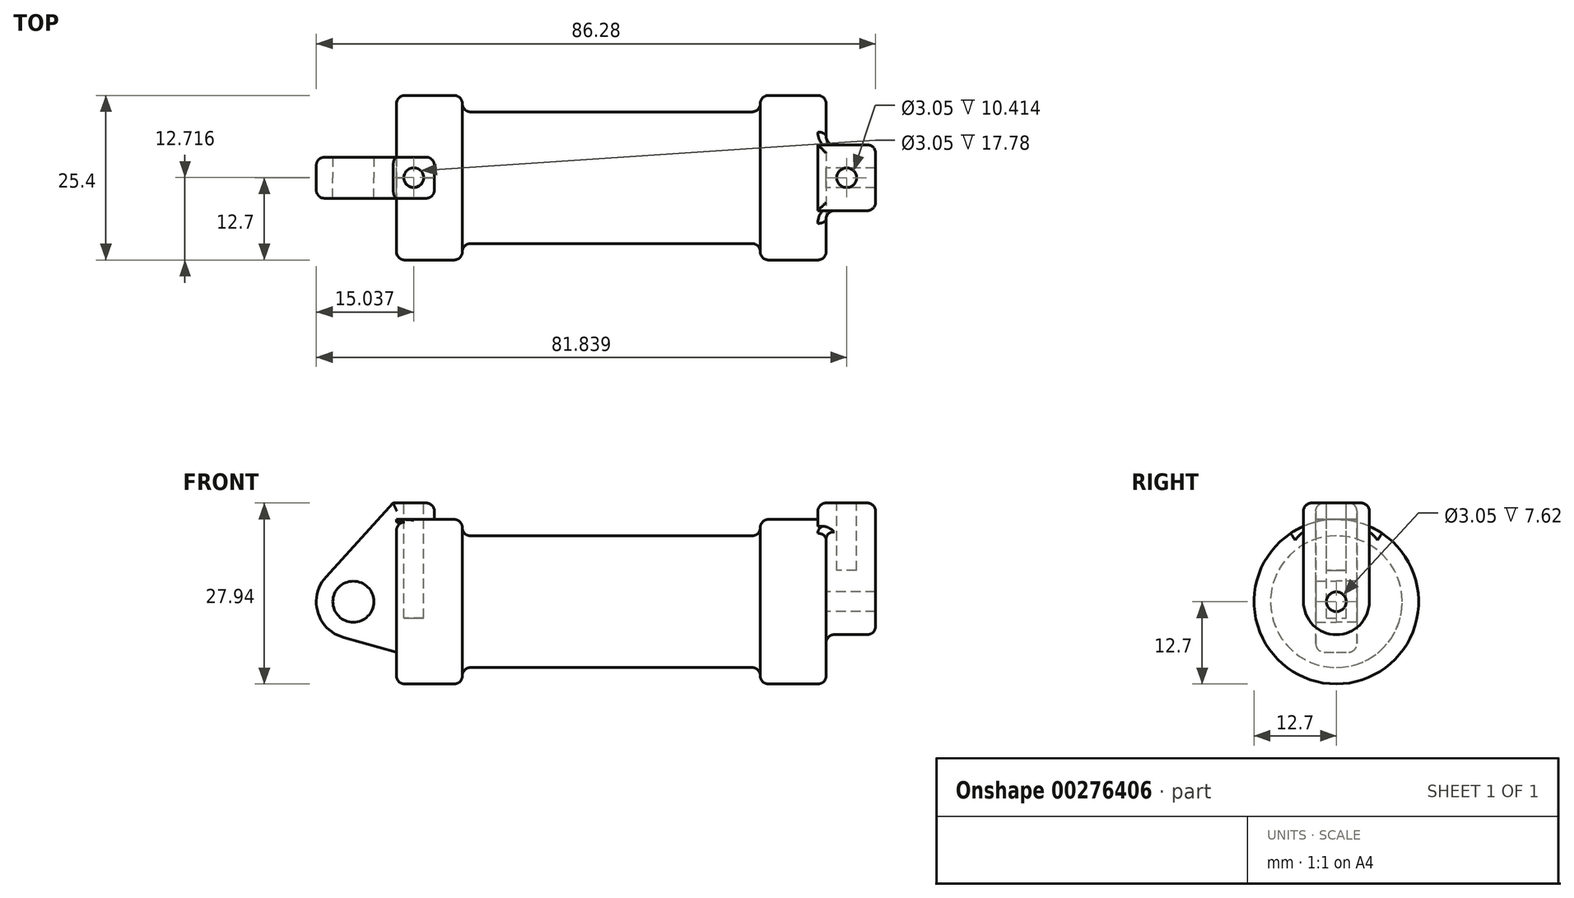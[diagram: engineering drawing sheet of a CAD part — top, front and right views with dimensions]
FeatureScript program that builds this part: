
annotation { "Feature Type Name" : "Feature", "Feature Type Description" : "" }
export const myFeature = defineFeature(function(context is Context, id is Id, definition is map)
    precondition{}
    {
        {
            var Q0;
            Q0=qCreatedBy(makeId("Front.planeOp"),FACE);
            var sketch = newSketch(context, id + "F0", { "sketchPlane" : qUnion([Q0])});
            skLineSegment(sketch, "E0", {"start": v(0, 0) * mm, "end": v(0, 12.7) * mm});
            skLineSegment(sketch, "E1", {"start": v(0, 12.7) * mm, "end": v(10.16, 12.7) * mm});
            skLineSegment(sketch, "E2", {"start": v(10.16, 12.7) * mm, "end": v(10.16, 10.16) * mm});
            skLineSegment(sketch, "E3", {"start": v(10.16, 10.16) * mm, "end": v(56.13, 10.16) * mm});
            skLineSegment(sketch, "E4", {"start": v(56.13, 10.16) * mm, "end": v(56.13, 12.7) * mm});
            skLineSegment(sketch, "E5", {"start": v(56.13, 12.7) * mm, "end": v(66.3, 12.7) * mm});
            skLineSegment(sketch, "E6", {"start": v(66.3, 12.7) * mm, "end": v(66.3, 0) * mm});
            skLineSegment(sketch, "E7", {"start": v(66.3, 0) * mm, "end": v(0, 0) * mm});
            skLineSegment(sketch, "E8", {"start": v(5.84, 15.24) * mm, "end": v(-0.5, 15.24) * mm});
            skLineSegment(sketch, "E9", {"start": v(-0.5, 15.24) * mm, "end": v(-10.88, 3.85) * mm});
            skLineSegment(sketch, "E10", {"start": v(0, 0) * mm, "end": v(-6.65, 0) * mm});
            skCircle(sketch, "E11", {"center": v(-6.65, 0) * mm, "radius": 5.72 * mm});
            skCircle(sketch, "E12", {"center": v(-6.65, 0) * mm, "radius": 3.18 * mm});
            skLineSegment(sketch, "E13", {"start": v(5.84, 15.24) * mm, "end": v(5.84, -9.4) * mm});
            skLineSegment(sketch, "E14", {"start": v(5.84, -9.4) * mm, "end": v(-8.18, -5.5) * mm});
            skSolve(sketch);
        }
        {
            var Q0;
            {var subQ0=sQuery(id+"F0.wireOp",EDGE,"E2");Q0=makeQuery(id+"F0.imprint","IMPRINT",FACE,{"disambiguationData":[TD([[makeQuery(id+"F0.imprint","IMPRINT",EDGE,{"derivedFrom":subQ0}),-1.0]])]});}
            var Q1;
            {var subQ0=sQuery(id+"F0.wireOp",EDGE,"E0");Q1=makeQuery(id+"F0.imprint","IMPRINT",FACE,{"disambiguationData":[TD([[makeQuery(id+"F0.imprint","IMPRINT",EDGE,{"derivedFrom":subQ0}),-1.0]])]});}
            var Q2;
            Q2=sQuery(id+"F0.wireOp",EDGE,"E7");
            revolve(context, id + "F1", {"entities" : qUnion([Q0, Q1]), "axis" : qUnion([Q2]), "revolveType" : RevolveType.FULL});
        }
        {
            var Q0;
            Q0=makeQuery(id+"F0.imprint","IMPRINT",FACE,{"disambiguationData":[TD([[makeQuery(id+"F0.imprint","IMPRINT",EDGE,{"derivedFrom":sQuery(id+"F0.wireOp",EDGE,"E12")}),-1.0]])]});
            var Q1;
            {var subQ0=sQuery(id+"F0.wireOp",EDGE,"E14");Q1=makeQuery(id+"F0.imprint","IMPRINT",FACE,{"disambiguationData":[TD([[makeQuery(id+"F0.imprint","IMPRINT",EDGE,{"derivedFrom":subQ0}),-1.0]])]});}
            var Q2;
            {var subQ1=sQuery(id+"F0.wireOp",EDGE,"E0");Q2=makeQuery(id+"F0.imprint","IMPRINT",FACE,{"disambiguationData":[TD([[makeQuery(id+"F0.imprint","IMPRINT",EDGE,{"derivedFrom":subQ1}),1.0]])]});}
            extrude(context, id + "F2", {"entities" : qUnion([Q0, Q1, Q2]), "operationType" : NewBodyOperationType.ADD, "endBound" : BoundingType.SYMMETRIC, "depth" : 6.35 * mm, "hasDraft" : true, "draftAngle" : 0.1 * degree, "hasSecondDirection" : true, "secondDirectionOppositeDirection" : true, "secondDirectionDepth" : 25.4 * mm});
        }
        {
            var Q0;
            Q0=makeQuery(id+"F1.opRevolve","SWEPT_FACE",FACE,{"disambiguationData":[OSD([sQuery(id+"F0.wireOp",EDGE,"E6")])]});
            var sketch = newSketch(context, id + "F3", { "sketchPlane" : qUnion([Q0])});
            skCircle(sketch, "E15", {"center": v(0, 0) * mm, "radius": 1.52 * mm});
            skCircle(sketch, "E16", {"center": v(0, 0) * mm, "radius": 5.08 * mm});
            skLineSegment(sketch, "E17", {"start": v(-5.08, 0) * mm, "end": v(-5.08, 15.24) * mm});
            skLineSegment(sketch, "E18", {"start": v(5.08, 0) * mm, "end": v(5.08, 15.24) * mm});
            skLineSegment(sketch, "E19", {"start": v(-5.08, 15.24) * mm, "end": v(5.08, 15.24) * mm});
            skSolve(sketch);
        }
        {
            var Q0;
            {var subQ0=sQuery(id+"F3.wireOp",EDGE,"E17");var subQ1=sQuery(id+"F3.wireOp",EDGE,"E16");var subQ2=makeQuery(id+"F3.imprint","INTERSECT",VERTEX,{"derivedFrom":[subQ1,subQ0]});Q0=makeQuery(id+"F3.imprint","IMPRINT",FACE,{"disambiguationData":[TD([[makeQuery(id+"F3.imprint","IMPRINT",EDGE,{"disambiguationData":[TD([[subQ2,1.0]])],"derivedFrom":subQ1}),-1.0]])]});}
            var Q1;
            {var subQ0=sQuery(id+"F3.wireOp",EDGE,"E19");Q1=makeQuery(id+"F3.imprint","IMPRINT",FACE,{"disambiguationData":[TD([[makeQuery(id+"F3.imprint","IMPRINT",EDGE,{"derivedFrom":subQ0}),-1.0]])]});}
            var Q2;
            Q2=makeQuery(id+"F3.imprint","IMPRINT",FACE,{"disambiguationData":[TD([[makeQuery(id+"F3.imprint","IMPRINT",EDGE,{"derivedFrom":sQuery(id+"F3.wireOp",EDGE,"E15")}),-1.0]])]});
            extrude(context, id + "F4", {"entities" : qUnion([Q0, Q1, Q2]), "operationType" : NewBodyOperationType.ADD, "depth" : 7.62 * mm});
        }
        {
            var Q0;
            Q0=makeQuery(id+"F4.opExtrude","CAP_FACE",FACE,{"disambiguationData":[OSD([sQuery(id+"F3.wireOp",EDGE,"E15"),sQuery(id+"F3.wireOp",EDGE,"E16"),sQuery(id+"F3.wireOp",EDGE,"E17"),sQuery(id+"F3.wireOp",EDGE,"E18"),sQuery(id+"F3.wireOp",EDGE,"E19")])],"isStart":true});
            extrude(context, id + "F5", {"entities" : qUnion([Q0]), "operationType" : NewBodyOperationType.ADD, "depth" : 1.27 * mm});
        }
        {
            var Q0;
            {var subQ0=sQuery(id+"F3.wireOp",EDGE,"E19");Q0=makeQuery(id+"F5.boolean.opBoolean","MERGE",FACE,{"derivedFrom":[makeQuery(id+"F4.opExtrude","SWEPT_FACE",FACE,{"disambiguationData":[OSD([subQ0])]}),makeQuery(id+"F5.opExtrude","SWEPT_FACE",FACE,{"disambiguationData":[OSD([subQ0])]})]});}
            var sketch = newSketch(context, id + "F6", { "sketchPlane" : qUnion([Q0])});
            skCircle(sketch, "E20", {"center": v(69.47, 0) * mm, "radius": 1.52 * mm});
            skSolve(sketch);
        }
        {
            var Q0;
            Q0=makeQuery(id+"F6.imprint","IMPRINT",FACE,{"disambiguationData":[TD([[makeQuery(id+"F6.imprint","IMPRINT",EDGE,{"derivedFrom":sQuery(id+"F6.wireOp",EDGE,"E20")}),1.0]])]});
            extrude(context, id + "F7", {"entities" : qUnion([Q0]), "operationType" : NewBodyOperationType.REMOVE, "oppositeDirection" : true, "depth" : 10.4 * mm});
        }
        {
            var Q0;
            Q0=makeQuery(id+"F1.opRevolve","SWEPT_EDGE",EDGE,{"disambiguationData":[OSD([sQuery(id+"F0.wireOp",EDGE,"E3"),sQuery(id+"F0.wireOp",EDGE,"E4")])]});
            var Q1;
            Q1=makeQuery(id+"F1.opRevolve","SWEPT_EDGE",EDGE,{"disambiguationData":[OSD([sQuery(id+"F0.wireOp",EDGE,"E4"),sQuery(id+"F0.wireOp",EDGE,"E5")])]});
            var Q2;
            Q2=makeQuery(id+"F5.opExtrude","CAP_EDGE",EDGE,{"disambiguationData":[OSD([sQuery(id+"F0.wireOp",EDGE,"E5"),sQuery(id+"F0.wireOp",EDGE,"E6")])],"isStart":false});
            var Q3;
            {var subQ0=sQuery(id+"F3.wireOp",EDGE,"E17");var subQ1=sQuery(id+"F3.wireOp",EDGE,"E19");var subQ2=sQuery(id+"F3.wireOp",EDGE,"E18");var subQ3=sQuery(id+"F3.wireOp",EDGE,"E16");var subQ4=sQuery(id+"F3.wireOp",EDGE,"E15");var subQ5=sQuery(id+"F0.wireOp",EDGE,"E6");var subQ6=sQuery(id+"F0.wireOp",EDGE,"E5");Q3=makeQuery(id+"F5.opExtrude","SWEPT_EDGE",EDGE,{"disambiguationData":[OSD([subQ6,subQ5,subQ4,subQ3,subQ0,subQ2,subQ1]),TDD([makeQuery(id+"F4.boolean.opBoolean","TWEAK_VERTEX",VERTEX,{"derivedFrom":[makeQuery(id+"F1.opRevolve","SWEPT_FACE",FACE,{"disambiguationData":[OSD([subQ6])]}),makeQuery(id+"F1.opRevolve","SWEPT_FACE",FACE,{"disambiguationData":[OSD([subQ5])]}),makeQuery(id+"F4.opExtrude","CAP_FACE",FACE,{"disambiguationData":[OSD([subQ4,subQ3,subQ0,subQ2,subQ1])],"isStart":true}),makeQuery(id+"F4.opExtrude","SWEPT_FACE",FACE,{"disambiguationData":[OSD([subQ0])]})]})])]});}
            var Q4;
            {var subQ0=sQuery(id+"F3.wireOp",EDGE,"E16");var subQ1=sQuery(id+"F3.wireOp",EDGE,"E17");Q4=makeQuery(id+"F4.boolean.opBoolean","SPLIT",EDGE,{"disambiguationData":[TD([makeQuery(id+"F4.opExtrude","SWEPT_FACE",FACE,{"disambiguationData":[OSD([subQ0])]})])],"derivedFrom":makeQuery(id+"F4.opExtrude","CAP_EDGE",EDGE,{"disambiguationData":[OSD([subQ1])],"isStart":true})});}
            var Q5;
            Q5=makeQuery(id+"F4.opExtrude","CAP_EDGE",EDGE,{"disambiguationData":[OSD([sQuery(id+"F3.wireOp",EDGE,"E16")])],"isStart":true});
            var Q6;
            {var subQ0=sQuery(id+"F3.wireOp",EDGE,"E16");var subQ1=sQuery(id+"F3.wireOp",EDGE,"E18");Q6=makeQuery(id+"F4.boolean.opBoolean","SPLIT",EDGE,{"disambiguationData":[TD([makeQuery(id+"F4.opExtrude","SWEPT_FACE",FACE,{"disambiguationData":[OSD([subQ0])]})])],"derivedFrom":makeQuery(id+"F4.opExtrude","CAP_EDGE",EDGE,{"disambiguationData":[OSD([subQ1])],"isStart":true})});}
            var Q7;
            {var subQ0=sQuery(id+"F3.wireOp",EDGE,"E18");var subQ1=sQuery(id+"F3.wireOp",EDGE,"E19");var subQ2=sQuery(id+"F3.wireOp",EDGE,"E17");var subQ3=sQuery(id+"F3.wireOp",EDGE,"E16");var subQ4=sQuery(id+"F3.wireOp",EDGE,"E15");var subQ5=sQuery(id+"F0.wireOp",EDGE,"E6");var subQ6=sQuery(id+"F0.wireOp",EDGE,"E5");Q7=makeQuery(id+"F5.opExtrude","SWEPT_EDGE",EDGE,{"disambiguationData":[OSD([subQ6,subQ5,subQ4,subQ3,subQ2,subQ0,subQ1]),TDD([makeQuery(id+"F4.boolean.opBoolean","TWEAK_VERTEX",VERTEX,{"derivedFrom":[makeQuery(id+"F1.opRevolve","SWEPT_FACE",FACE,{"disambiguationData":[OSD([subQ6])]}),makeQuery(id+"F1.opRevolve","SWEPT_FACE",FACE,{"disambiguationData":[OSD([subQ5])]}),makeQuery(id+"F4.opExtrude","CAP_FACE",FACE,{"disambiguationData":[OSD([subQ4,subQ3,subQ2,subQ0,subQ1])],"isStart":true}),makeQuery(id+"F4.opExtrude","SWEPT_FACE",FACE,{"disambiguationData":[OSD([subQ0])]})]})])]});}
            var Q8;
            Q8=makeQuery(id+"F5.opExtrude","CAP_EDGE",EDGE,{"disambiguationData":[OSD([sQuery(id+"F3.wireOp",EDGE,"E19")])],"isStart":false});
            var Q9;
            {var subQ0=sQuery(id+"F3.wireOp",EDGE,"E19");var subQ1=sQuery(id+"F3.wireOp",EDGE,"E17");Q9=makeQuery(id+"F5.boolean.opBoolean","MERGE",EDGE,{"derivedFrom":[makeQuery(id+"F4.opExtrude","SWEPT_EDGE",EDGE,{"disambiguationData":[OSD([subQ1,subQ0])]}),makeQuery(id+"F5.opExtrude","SWEPT_EDGE",EDGE,{"disambiguationData":[OSD([subQ1,subQ0])]})]});}
            var Q10;
            Q10=makeQuery(id+"F4.opExtrude","CAP_EDGE",EDGE,{"disambiguationData":[OSD([sQuery(id+"F3.wireOp",EDGE,"E19")])],"isStart":false});
            var Q11;
            {var subQ0=sQuery(id+"F3.wireOp",EDGE,"E19");var subQ1=sQuery(id+"F3.wireOp",EDGE,"E18");Q11=makeQuery(id+"F5.boolean.opBoolean","MERGE",EDGE,{"derivedFrom":[makeQuery(id+"F4.opExtrude","SWEPT_EDGE",EDGE,{"disambiguationData":[OSD([subQ1,subQ0])]}),makeQuery(id+"F5.opExtrude","SWEPT_EDGE",EDGE,{"disambiguationData":[OSD([subQ1,subQ0])]})]});}
            var Q12;
            Q12=makeQuery(id+"F4.opExtrude","CAP_EDGE",EDGE,{"disambiguationData":[OSD([sQuery(id+"F3.wireOp",EDGE,"E17")])],"isStart":false});
            var Q13;
            Q13=makeQuery(id+"F4.opExtrude","CAP_EDGE",EDGE,{"disambiguationData":[OSD([sQuery(id+"F3.wireOp",EDGE,"E16")])],"isStart":false});
            var Q14;
            Q14=makeQuery(id+"F4.opExtrude","CAP_EDGE",EDGE,{"disambiguationData":[OSD([sQuery(id+"F3.wireOp",EDGE,"E18")])],"isStart":false});
            fillet(context, id + "F8", {"entities" : qUnion([Q0, Q1, Q2, Q3, Q4, Q5, Q6, Q7, Q8, Q9, Q10, Q11, Q12, Q13, Q14]), "radius" : 1.27 * mm, "tangentPropagation" : true, "allowEdgeOverflow" : false});
        }
        {
            var Q0;
            Q0=makeQuery(id+"F4.boolean.opBoolean","SPLIT",EDGE,{"disambiguationData":[OD(1.0)],"derivedFrom":makeQuery(id+"F1.opRevolve","SWEPT_EDGE",EDGE,{"disambiguationData":[OSD([sQuery(id+"F0.wireOp",EDGE,"E5"),sQuery(id+"F0.wireOp",EDGE,"E6")])]})});
            fillet(context, id + "F9", {"entities" : qUnion([Q0]), "radius" : 1.27 * mm, "tangentPropagation" : true, "allowEdgeOverflow" : false});
        }
        {
            var Q0;
            Q0=makeQuery(id+"F2.*.split.splitOp","SPLIT",FACE,{"derivedFrom":makeQuery(id+"F2.opExtrude","SWEPT_FACE",FACE,{"disambiguationData":[OSD([sQuery(id+"F0.wireOp",EDGE,"E8")])]}),"isFromBackBody":true});
            var sketch = newSketch(context, id + "F10", { "sketchPlane" : qUnion([Q0])});
            skCircle(sketch, "E21", {"center": v(2.67, 0.03) * mm, "radius": 1.52 * mm});
            skSolve(sketch);
        }
        {
            var Q0;
            Q0 = qSketchRegion(id + "F10", true);
            extrude(context, id + "F11", {"entities" : qUnion([Q0]), "operationType" : NewBodyOperationType.REMOVE, "oppositeDirection" : true, "depth" : 17.78 * mm});
        }
        {
            var Q0;
            Q0=makeQuery(id+"F1.opRevolve","SWEPT_EDGE",EDGE,{"disambiguationData":[OSD([sQuery(id+"F0.wireOp",EDGE,"E2"),sQuery(id+"F0.wireOp",EDGE,"E3")])]});
            var Q1;
            Q1=makeQuery(id+"F1.opRevolve","SWEPT_EDGE",EDGE,{"disambiguationData":[OSD([sQuery(id+"F0.wireOp",EDGE,"E1"),sQuery(id+"F0.wireOp",EDGE,"E2")])]});
            var Q2;
            Q2=makeQuery(id+"F1.opRevolve","SWEPT_EDGE",EDGE,{"disambiguationData":[OSD([sQuery(id+"F0.wireOp",EDGE,"E0"),sQuery(id+"F0.wireOp",EDGE,"E1")])]});
            var Q3;
            Q3=makeQuery(id+"F2.opExtrude","CAP_EDGE",EDGE,{"disambiguationData":[OSD([sQuery(id+"F0.wireOp",EDGE,"E14")])],"isStart":false});
            var Q4;
            Q4=makeQuery(id+"F2.opExtrude","CAP_EDGE",EDGE,{"disambiguationData":[OSD([sQuery(id+"F0.wireOp",EDGE,"E8")])],"isStart":false});
            var Q5;
            Q5=makeQuery(id+"F2.*.split.splitOp","SPLIT",EDGE,{"derivedFrom":makeQuery(id+"F2.opExtrude","SWEPT_EDGE",EDGE,{"disambiguationData":[OSD([sQuery(id+"F0.wireOp",EDGE,"E8"),sQuery(id+"F0.wireOp",EDGE,"E13")])]})});
            var Q6;
            Q6=makeQuery(id+"F2.*.split.splitOp","SPLIT",EDGE,{"derivedFrom":makeQuery(id+"F2.opExtrude","SWEPT_EDGE",EDGE,{"disambiguationData":[OSD([sQuery(id+"F0.wireOp",EDGE,"E8"),sQuery(id+"F0.wireOp",EDGE,"E13")])]}),"isFromBackBody":true});
            var Q7;
            {var subQ0=sQuery(id+"F0.wireOp",EDGE,"E13");Q7=makeQuery(id+"F2.opExtrude","CAP_EDGE",EDGE,{"disambiguationData":[OSD([subQ0]),TDD([makeQuery(id+"F0.imprint","IMPRINT",EDGE,{"disambiguationData":[TD([[makeQuery(id+"F0.imprint","INTERSECT",VERTEX,{"derivedFrom":[sQuery(id+"F0.wireOp",EDGE,"E8"),subQ0]}),-1.0]])],"derivedFrom":subQ0})])],"isStart":true});}
            var Q8;
            Q8=makeQuery(id+"F2.opExtrude","CAP_EDGE",EDGE,{"disambiguationData":[OSD([sQuery(id+"F0.wireOp",EDGE,"E8")])],"isStart":true});
            var Q9;
            Q9=makeQuery(id+"F2.opExtrude","CAP_EDGE",EDGE,{"disambiguationData":[OSD([sQuery(id+"F0.wireOp",EDGE,"E14")])],"isStart":true});
            var Q10;
            {var subQ0=sQuery(id+"F0.wireOp",EDGE,"E13");Q10=makeQuery(id+"F2.opExtrude","CAP_EDGE",EDGE,{"disambiguationData":[OSD([subQ0]),TDD([makeQuery(id+"F0.imprint","IMPRINT",EDGE,{"disambiguationData":[TD([[makeQuery(id+"F0.imprint","INTERSECT",VERTEX,{"derivedFrom":[sQuery(id+"F0.wireOp",EDGE,"E8"),subQ0]}),-1.0]])],"derivedFrom":subQ0})])],"isStart":false});}
            fillet(context, id + "F12", {"entities" : qUnion([Q0, Q1, Q2, Q3, Q4, Q5, Q6, Q7, Q8, Q9, Q10]), "radius" : 1.27 * mm, "tangentPropagation" : true, "allowEdgeOverflow" : false});
        }
    });
